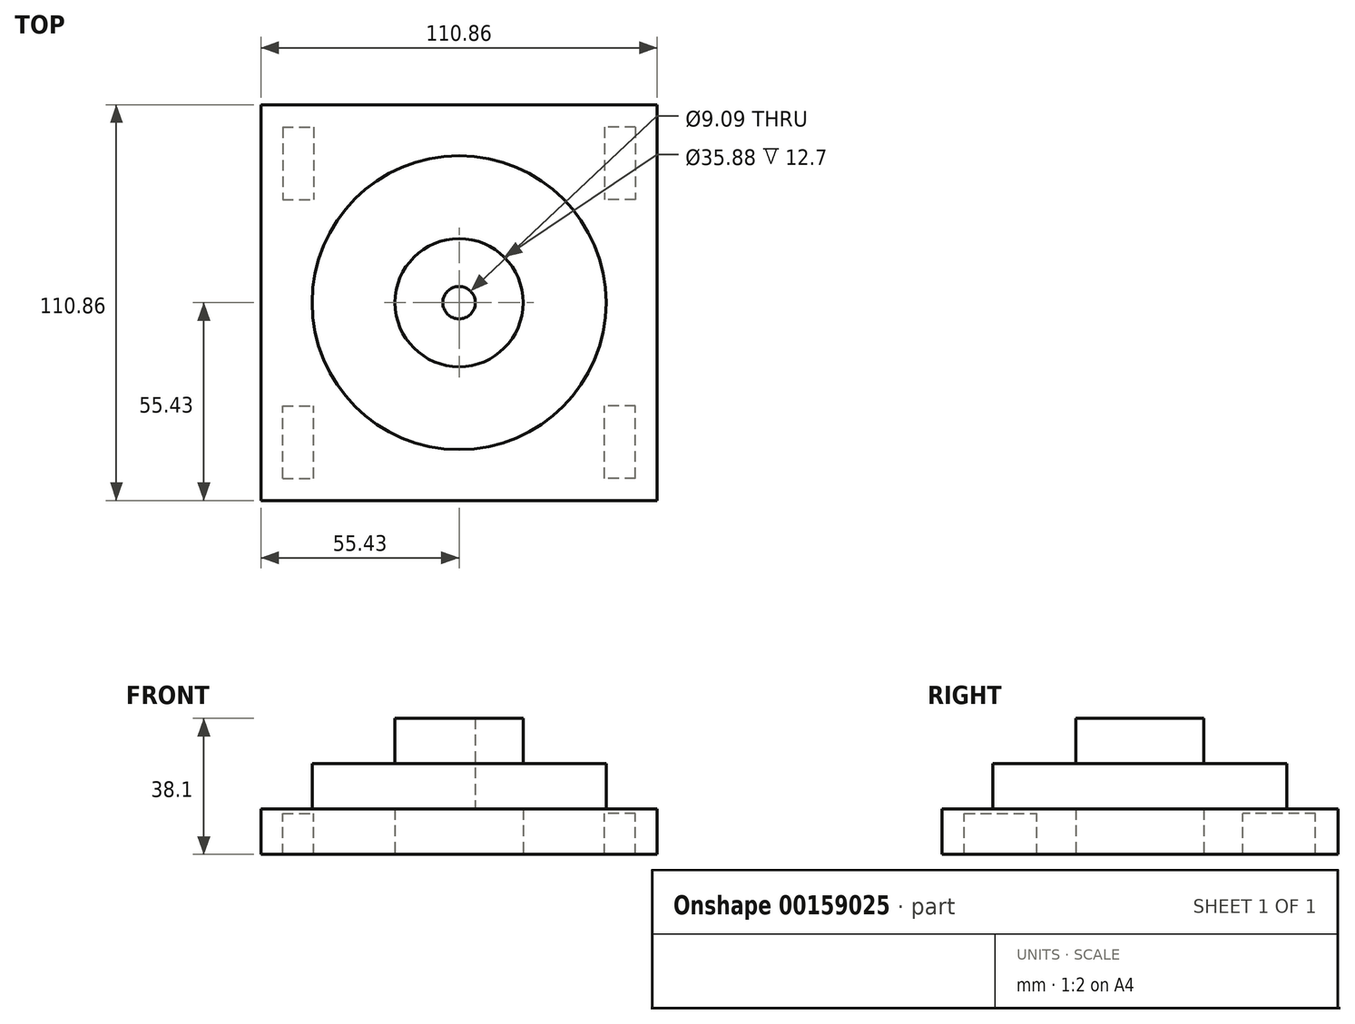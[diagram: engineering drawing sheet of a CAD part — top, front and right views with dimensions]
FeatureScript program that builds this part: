
annotation { "Feature Type Name" : "Feature", "Feature Type Description" : "" }
export const myFeature = defineFeature(function(context is Context, id is Id, definition is map)
    precondition{}
    {
        {
            var Q0;
            Q0=qCreatedBy(makeId("Top.planeOp"),FACE);
            var sketch = newSketch(context, id + "F0", { "sketchPlane" : qUnion([Q0])});
            skCircle(sketch, "E0", {"center": v(0, 0) * mm, "radius": 41.15 * mm});
            skCircle(sketch, "E1", {"center": v(0, 0) * mm, "radius": 17.94 * mm});
            skCircle(sketch, "E2", {"center": v(0, 0) * mm, "radius": 4.55 * mm});
            skLineSegment(sketch, "E3", {"start": v(55.43, -55.43) * mm, "end": v(-55.43, -55.43) * mm});
            skLineSegment(sketch, "E4", {"start": v(-55.43, -55.43) * mm, "end": v(-55.43, 55.43) * mm});
            skLineSegment(sketch, "E5", {"start": v(-55.43, 55.43) * mm, "end": v(55.43, 55.43) * mm});
            skLineSegment(sketch, "E6", {"start": v(55.43, -55.43) * mm, "end": v(55.43, 55.43) * mm});
            skLineSegment(sketch, "E7.bottom", {"start": v(49.37, 49.18) * mm, "end": v(40.65, 49.18) * mm});
            skLineSegment(sketch, "E7.top", {"start": v(49.37, 28.86) * mm, "end": v(40.65, 28.86) * mm});
            skLineSegment(sketch, "E7.left", {"start": v(49.37, 49.18) * mm, "end": v(49.37, 28.86) * mm});
            skLineSegment(sketch, "E7.right", {"start": v(40.65, 49.18) * mm, "end": v(40.65, 28.86) * mm});
            skLineSegment(sketch, "E8.MirrorCS", {"start": v(-40.65, 49.18) * mm, "end": v(-40.65, 28.86) * mm});
            skLineSegment(sketch, "E9.MirrorCS", {"start": v(-49.37, 49.18) * mm, "end": v(-40.65, 49.18) * mm});
            skLineSegment(sketch, "E10.MirrorCS", {"start": v(-49.37, 28.86) * mm, "end": v(-40.65, 28.86) * mm});
            skLineSegment(sketch, "E11.MirrorCS", {"start": v(-49.37, 49.18) * mm, "end": v(-49.37, 28.86) * mm});
            skLineSegment(sketch, "E12.MirrorCS", {"start": v(-49.37, -49.18) * mm, "end": v(-40.65, -49.18) * mm});
            skLineSegment(sketch, "E13.MirrorCS", {"start": v(-49.37, -49.18) * mm, "end": v(-49.37, -28.86) * mm});
            skLineSegment(sketch, "E14.MirrorCS", {"start": v(-49.37, -28.86) * mm, "end": v(-40.65, -28.86) * mm});
            skLineSegment(sketch, "E15.MirrorCS", {"start": v(-40.65, -49.18) * mm, "end": v(-40.65, -28.86) * mm});
            skLineSegment(sketch, "E16.MirrorCS", {"start": v(40.65, -49.18) * mm, "end": v(40.65, -28.86) * mm});
            skLineSegment(sketch, "E17.MirrorCS", {"start": v(49.37, -49.18) * mm, "end": v(40.65, -49.18) * mm});
            skLineSegment(sketch, "E18.MirrorCS", {"start": v(49.37, -28.86) * mm, "end": v(40.65, -28.86) * mm});
            skLineSegment(sketch, "E19.MirrorCS", {"start": v(49.37, -49.18) * mm, "end": v(49.37, -28.86) * mm});
            skSolve(sketch);
        }
        {
            var Q0;
            Q0=makeQuery(id+"F0.imprint","IMPRINT",FACE,{"disambiguationData":[TD([[makeQuery(id+"F0.imprint","IMPRINT",EDGE,{"derivedFrom":sQuery(id+"F0.wireOp",EDGE,"E1")}),1.0]])]});
            extrude(context, id + "F1", {"entities" : qUnion([Q0]), "depth" : 25.4 * mm});
        }
        {
            var Q0;
            Q0=makeQuery(id+"F0.imprint","IMPRINT",FACE,{"disambiguationData":[TD([[makeQuery(id+"F0.imprint","IMPRINT",EDGE,{"derivedFrom":sQuery(id+"F0.wireOp",EDGE,"E0")}),1.0]])]});
            extrude(context, id + "F2", {"entities" : qUnion([Q0]), "operationType" : NewBodyOperationType.ADD, "endBound" : BoundingType.SYMMETRIC, "depth" : 25.4 * mm});
        }
        {
            var Q0;
            Q0=makeQuery(id+"F0.imprint","IMPRINT",FACE,{"disambiguationData":[TD([[makeQuery(id+"F0.imprint","IMPRINT",EDGE,{"derivedFrom":sQuery(id+"F0.wireOp",EDGE,"E0")}),-1.0]])]});
            extrude(context, id + "F3", {"entities" : qUnion([Q0]), "operationType" : NewBodyOperationType.ADD, "oppositeDirection" : true, "depth" : 12.7 * mm});
        }
        {
            var Q0;
            Q0=makeQuery(id+"F0.imprint","IMPRINT",FACE,{"disambiguationData":[TD([[makeQuery(id+"F0.imprint","IMPRINT",EDGE,{"derivedFrom":sQuery(id+"F0.wireOp",EDGE,"E8.MirrorCS")}),-1.0]])]});
            var Q1;
            Q1=makeQuery(id+"F0.imprint","IMPRINT",FACE,{"disambiguationData":[TD([[makeQuery(id+"F0.imprint","IMPRINT",EDGE,{"derivedFrom":sQuery(id+"F0.wireOp",EDGE,"E7.right")}),1.0]])]});
            var Q2;
            Q2=makeQuery(id+"F0.imprint","IMPRINT",FACE,{"disambiguationData":[TD([[makeQuery(id+"F0.imprint","IMPRINT",EDGE,{"derivedFrom":sQuery(id+"F0.wireOp",EDGE,"E16.MirrorCS")}),-1.0]])]});
            var Q3;
            Q3=makeQuery(id+"F0.imprint","IMPRINT",FACE,{"disambiguationData":[TD([[makeQuery(id+"F0.imprint","IMPRINT",EDGE,{"derivedFrom":sQuery(id+"F0.wireOp",EDGE,"E12.MirrorCS")}),1.0]])]});
            extrude(context, id + "F4", {"entities" : qUnion([Q0, Q1, Q2, Q3]), "operationType" : NewBodyOperationType.ADD, "oppositeDirection" : true, "depth" : 1.27 * mm});
        }
    });
